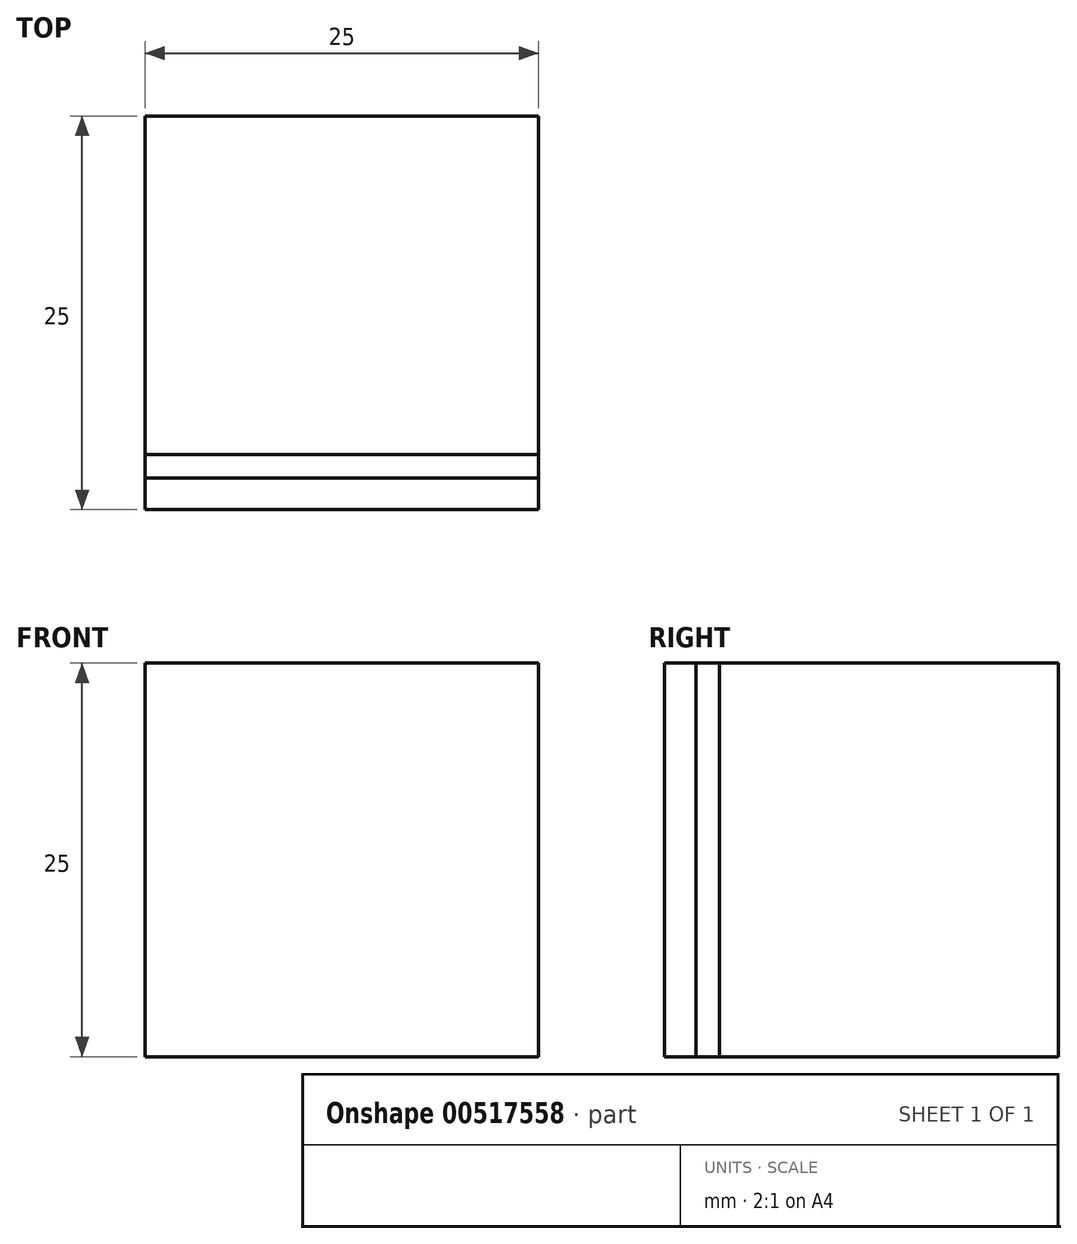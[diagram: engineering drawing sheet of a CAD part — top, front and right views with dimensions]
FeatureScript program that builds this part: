
annotation { "Feature Type Name" : "Feature", "Feature Type Description" : "" }
export const myFeature = defineFeature(function(context is Context, id is Id, definition is map)
    precondition{}
    {
        {
            var Q0;
            Q0=qCreatedBy(makeId("Front.planeOp"),FACE);
            var sketch = newSketch(context, id + "F0", { "sketchPlane" : qUnion([Q0])});
            skLineSegment(sketch, "E0.bottom", {"start": v(25, 25) * mm, "end": v(0, 25) * mm});
            skLineSegment(sketch, "E0.top", {"start": v(25, 0) * mm, "end": v(0, 0) * mm});
            skLineSegment(sketch, "E0.left", {"start": v(25, 25) * mm, "end": v(25, 0) * mm});
            skLineSegment(sketch, "E0.right", {"start": v(0, 25) * mm, "end": v(0, 0) * mm});
            skSolve(sketch);
        }
        {
            var Q0;
            Q0 = qSketchRegion(id + "F0", true);
            extrude(context, id + "F1", {"entities" : qUnion([Q0]), "depth" : 25 * mm, "offsetDistance" : 25 * mm});
        }
        {
            var Q0;
            Q0=makeQuery(id+"F1.opExtrude","SWEPT_FACE",FACE,{"disambiguationData":[OSD([sQuery(id+"F0.wireOp",EDGE,"E0.left")])]});
            var sketch = newSketch(context, id + "F2", { "sketchPlane" : qUnion([Q0])});
            skLineSegment(sketch, "E1", {"start": v(-23, 25) * mm, "end": v(-23, 0) * mm});
            skLineSegment(sketch, "E2", {"start": v(-23, 0) * mm, "end": v(-21.5, 0) * mm});
            skLineSegment(sketch, "E3", {"start": v(-21.5, 0) * mm, "end": v(-21.5, 25) * mm});
            skLineSegment(sketch, "E4", {"start": v(-21.5, 25) * mm, "end": v(-23, 25) * mm});
            skSolve(sketch);
        }
        {
            var Q0;
            Q0 = qSketchRegion(id + "F2", true);
            extrude(context, id + "F3", {"entities" : qUnion([Q0]), "operationType" : NewBodyOperationType.REMOVE, "oppositeDirection" : true, "depth" : 25 * mm, "offsetDistance" : 25 * mm});
        }
        {
            var Q0;
            Q0 = qSketchRegion(id + "F2", true);
            extrude(context, id + "F4", {"entities" : qUnion([Q0]), "oppositeDirection" : true, "depth" : 25 * mm, "offsetDistance" : 25 * mm});
        }
    });
